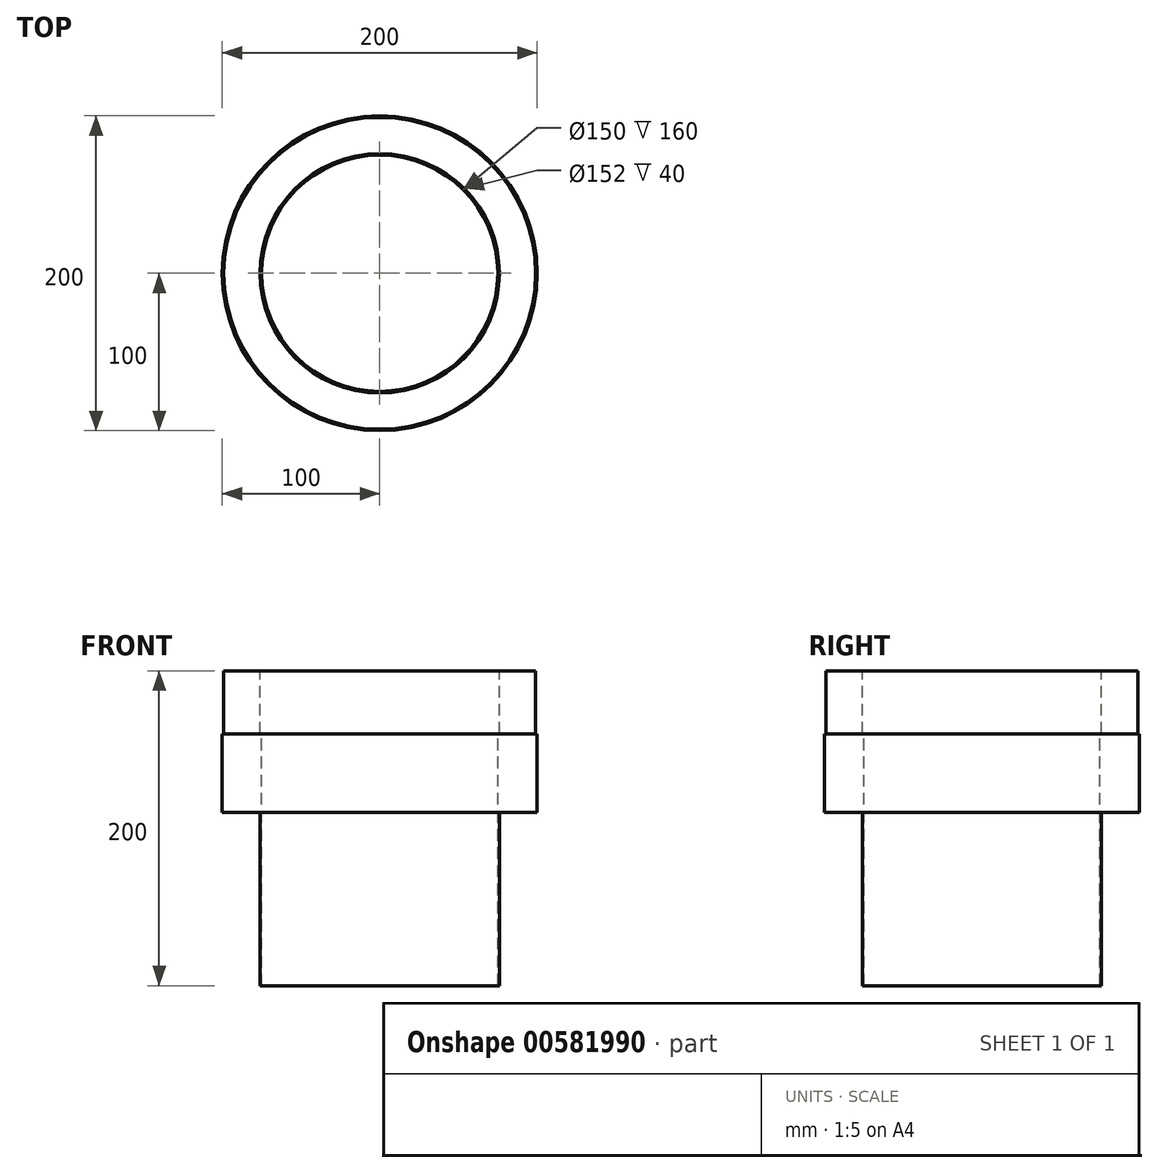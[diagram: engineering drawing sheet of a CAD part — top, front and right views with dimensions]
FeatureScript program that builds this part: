
annotation { "Feature Type Name" : "Feature", "Feature Type Description" : "" }
export const myFeature = defineFeature(function(context is Context, id is Id, definition is map)
    precondition{}
    {
        {
            var Q0;
            Q0=qCreatedBy(makeId("Front.planeOp"),FACE);
            var sketch = newSketch(context, id + "F0", { "sketchPlane" : qUnion([Q0])});
            skLineSegment(sketch, "E0", {"start": v(0, 710.75) * mm, "end": v(0, -704.58) * mm, "construction": true});
            skLineSegment(sketch, "E1", {"start": v(-75, 300.65) * mm, "end": v(-75, 410.65) * mm});
            skLineSegment(sketch, "E2", {"start": v(-75, 410.65) * mm, "end": v(-76, 410.65) * mm});
            skLineSegment(sketch, "E3", {"start": v(-99, 410.65) * mm, "end": v(-100, 410.65) * mm});
            skLineSegment(sketch, "E4", {"start": v(-100, 410.65) * mm, "end": v(-100, 360.65) * mm});
            skLineSegment(sketch, "E5", {"start": v(-100, 360.65) * mm, "end": v(-76, 360.65) * mm});
            skLineSegment(sketch, "E6", {"start": v(-76, 360.65) * mm, "end": v(-76, 300.65) * mm});
            skLineSegment(sketch, "E7", {"start": v(-99, 450.65) * mm, "end": v(-99, 410.65) * mm});
            skLineSegment(sketch, "E8", {"start": v(-99, 450.65) * mm, "end": v(-76, 450.65) * mm});
            skLineSegment(sketch, "E9", {"start": v(-76, 410.65) * mm, "end": v(-76, 450.65) * mm});
            skLineSegment(sketch, "E10", {"start": v(-75, 300.65) * mm, "end": v(-75, 250.65) * mm});
            skLineSegment(sketch, "E11", {"start": v(-76, 300.65) * mm, "end": v(-76, 250.65) * mm});
            skLineSegment(sketch, "E12", {"start": v(-76, 250.65) * mm, "end": v(-75, 250.65) * mm});
            skSolve(sketch);
        }
        {
            var Q0;
            Q0=qSketchRegion(id+"F0",true);
            var Q1;
            Q1=sQuery(id+"F0.wireOp",EDGE,"E0");
            revolve(context, id + "F1", {"entities" : qUnion([Q0]), "axis" : qUnion([Q1]), "revolveType" : RevolveType.FULL});
        }
    });
